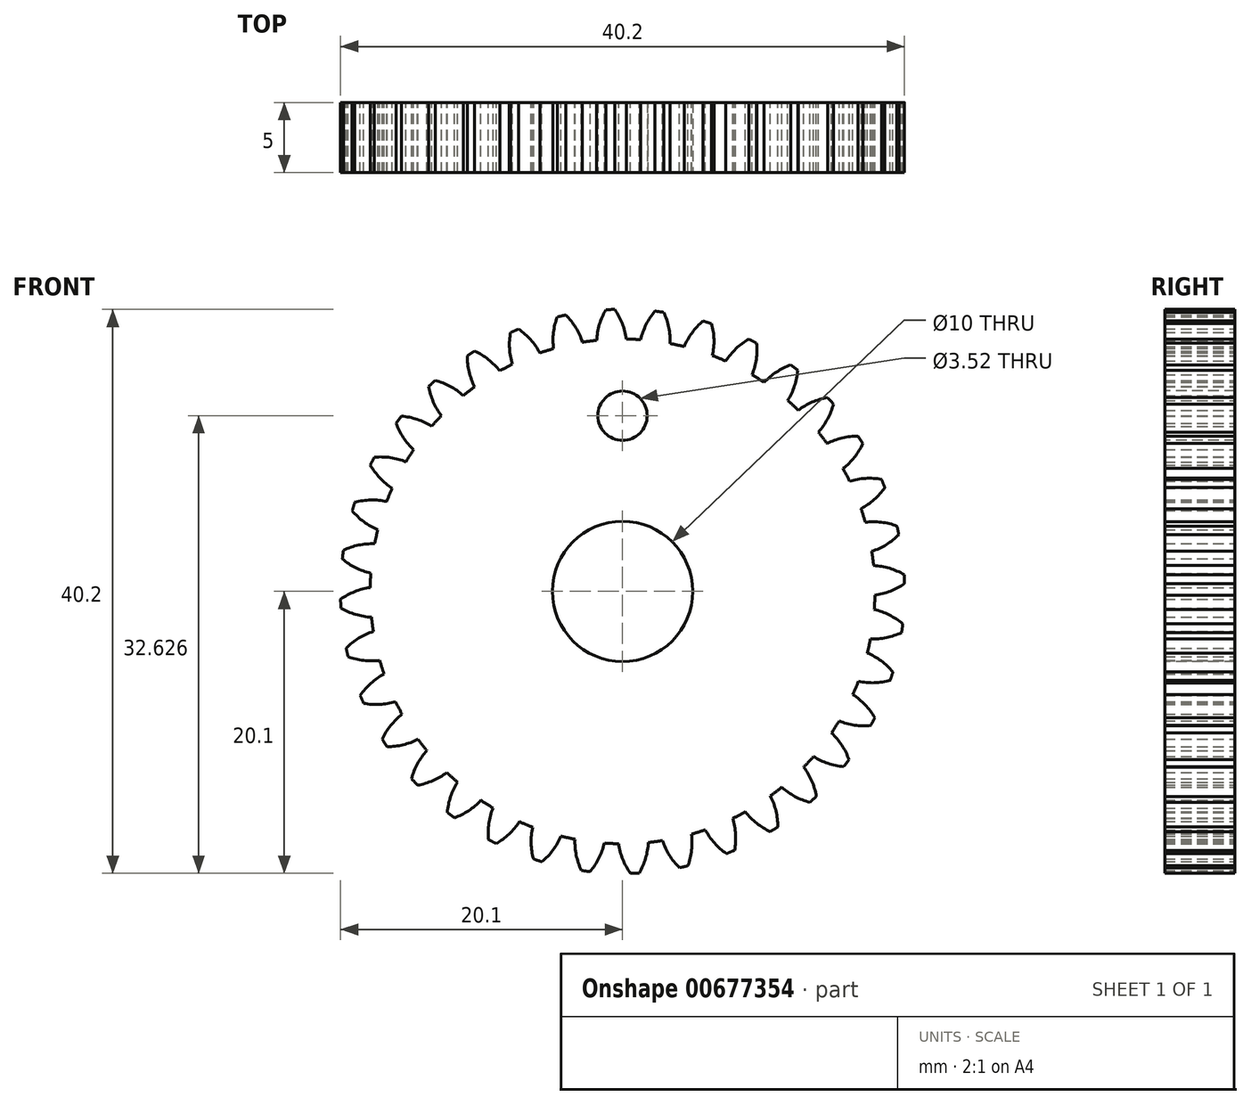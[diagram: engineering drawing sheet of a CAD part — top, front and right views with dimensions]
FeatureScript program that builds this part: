
annotation { "Feature Type Name" : "Feature", "Feature Type Description" : "" }
export const myFeature = defineFeature(function(context is Context, id is Id, definition is map)
    precondition{}
    {
        {
            var Q0;
            Q0=qCreatedBy(makeId("Front.planeOp"),FACE);
            var sketch = newSketch(context, id + "F0", { "sketchPlane" : qUnion([Q0])});
            skLineSegment(sketch, "E0", {"start": v(0, 0) * mm, "end": v(-1.18, 26.95) * mm, "construction": true});
            skArc(sketch, "E1.trimOffspring", {"start": v(0.27, 17.99) * mm, "mid": v(-0.02, 19.1) * mm, "end": v(-0.56, 20.1) * mm});
            skArc(sketch, "E2", {"start": v(-0.56, 20.1) * mm, "mid": v(-0.72, 20.1) * mm, "end": v(-0.88, 20.09) * mm});
            skArc(sketch, "E3.MirrorCS", {"start": v(-1.2, 20.07) * mm, "mid": v(-1.03, 20.08) * mm, "end": v(-0.88, 20.09) * mm});
            skArc(sketch, "E4.MirrorCS", {"start": v(-1.84, 17.9) * mm, "mid": v(-1.65, 19.02) * mm, "end": v(-1.2, 20.07) * mm});
            skArc(sketch, "E5.1.0", {"start": v(-2.85, 17.76) * mm, "mid": v(-3.33, 18.8) * mm, "end": v(-4.05, 19.7) * mm});
            skArc(sketch, "E5.1.1", {"start": v(-4.05, 19.7) * mm, "mid": v(-4.2, 19.66) * mm, "end": v(-4.35, 19.63) * mm});
            skArc(sketch, "E5.1.2", {"start": v(-4.92, 17.3) * mm, "mid": v(-4.93, 18.45) * mm, "end": v(-4.66, 19.56) * mm});
            skArc(sketch, "E5.1.3", {"start": v(-4.66, 19.56) * mm, "mid": v(-4.5, 19.6) * mm, "end": v(-4.35, 19.63) * mm});
            skArc(sketch, "E5.2.0", {"start": v(-5.9, 17) * mm, "mid": v(-6.55, 17.94) * mm, "end": v(-7.4, 18.7) * mm});
            skArc(sketch, "E5.2.1", {"start": v(-7.4, 18.7) * mm, "mid": v(-7.55, 18.64) * mm, "end": v(-7.7, 18.58) * mm});
            skArc(sketch, "E5.2.2", {"start": v(-7.85, 16.19) * mm, "mid": v(-8.05, 17.31) * mm, "end": v(-7.98, 18.46) * mm});
            skArc(sketch, "E5.2.3", {"start": v(-7.98, 18.46) * mm, "mid": v(-7.84, 18.52) * mm, "end": v(-7.7, 18.58) * mm});
            skArc(sketch, "E5.3.0", {"start": v(-8.76, 15.71) * mm, "mid": v(-9.56, 16.53) * mm, "end": v(-10.54, 17.13) * mm});
            skArc(sketch, "E5.3.1", {"start": v(-10.54, 17.13) * mm, "mid": v(-10.67, 17.04) * mm, "end": v(-10.8, 16.96) * mm});
            skArc(sketch, "E5.3.2", {"start": v(-10.54, 14.58) * mm, "mid": v(-10.94, 15.65) * mm, "end": v(-11.07, 16.79) * mm});
            skArc(sketch, "E5.3.3", {"start": v(-11.07, 16.79) * mm, "mid": v(-10.94, 16.87) * mm, "end": v(-10.8, 16.96) * mm});
            skArc(sketch, "E5.4.0", {"start": v(-11.35, 13.96) * mm, "mid": v(-12.29, 14.62) * mm, "end": v(-13.35, 15.04) * mm});
            skArc(sketch, "E5.4.1", {"start": v(-13.35, 15.04) * mm, "mid": v(-13.47, 14.93) * mm, "end": v(-13.58, 14.83) * mm});
            skArc(sketch, "E5.4.2", {"start": v(-12.91, 12.53) * mm, "mid": v(-13.49, 13.51) * mm, "end": v(-13.81, 14.61) * mm});
            skArc(sketch, "E5.4.3", {"start": v(-13.81, 14.61) * mm, "mid": v(-13.7, 14.72) * mm, "end": v(-13.58, 14.83) * mm});
            skArc(sketch, "E5.5.0", {"start": v(-13.6, 11.77) * mm, "mid": v(-14.64, 12.26) * mm, "end": v(-15.76, 12.49) * mm});
            skArc(sketch, "E5.5.1", {"start": v(-15.76, 12.49) * mm, "mid": v(-15.86, 12.37) * mm, "end": v(-15.95, 12.24) * mm});
            skArc(sketch, "E5.5.2", {"start": v(-14.9, 10.1) * mm, "mid": v(-15.63, 10.97) * mm, "end": v(-16.14, 12) * mm});
            skArc(sketch, "E5.5.3", {"start": v(-16.14, 12) * mm, "mid": v(-16.05, 12.12) * mm, "end": v(-15.95, 12.24) * mm});
            skArc(sketch, "E5.6.0", {"start": v(-15.44, 9.23) * mm, "mid": v(-16.55, 9.53) * mm, "end": v(-17.69, 9.56) * mm});
            skArc(sketch, "E5.6.1", {"start": v(-17.69, 9.56) * mm, "mid": v(-17.76, 9.42) * mm, "end": v(-17.84, 9.28) * mm});
            skArc(sketch, "E5.6.2", {"start": v(-16.42, 7.35) * mm, "mid": v(-17.3, 8.09) * mm, "end": v(-17.98, 9) * mm});
            skArc(sketch, "E5.6.3", {"start": v(-17.98, 9) * mm, "mid": v(-17.9, 9.15) * mm, "end": v(-17.84, 9.28) * mm});
            skArc(sketch, "E5.7.0", {"start": v(-16.8, 6.4) * mm, "mid": v(-17.95, 6.51) * mm, "end": v(-19.08, 6.34) * mm});
            skArc(sketch, "E5.7.1", {"start": v(-19.08, 6.34) * mm, "mid": v(-19.13, 6.2) * mm, "end": v(-19.18, 6.05) * mm});
            skArc(sketch, "E5.7.2", {"start": v(-17.45, 4.4) * mm, "mid": v(-18.44, 4.96) * mm, "end": v(-19.27, 5.75) * mm});
            skArc(sketch, "E5.7.3", {"start": v(-19.27, 5.75) * mm, "mid": v(-19.22, 5.9) * mm, "end": v(-19.18, 6.05) * mm});
            skArc(sketch, "E5.8.0", {"start": v(-17.67, 3.4) * mm, "mid": v(-18.8, 3.3) * mm, "end": v(-19.9, 2.94) * mm});
            skArc(sketch, "E5.8.1", {"start": v(-19.9, 2.94) * mm, "mid": v(-19.92, 2.78) * mm, "end": v(-19.94, 2.62) * mm});
            skArc(sketch, "E5.8.2", {"start": v(-17.94, 1.3) * mm, "mid": v(-19.02, 1.68) * mm, "end": v(-19.97, 2.31) * mm});
            skArc(sketch, "E5.8.3", {"start": v(-19.97, 2.31) * mm, "mid": v(-19.96, 2.47) * mm, "end": v(-19.94, 2.62) * mm});
            skArc(sketch, "E5.9.0", {"start": v(-17.99, 0.27) * mm, "mid": v(-19.1, -0.02) * mm, "end": v(-20.1, -0.56) * mm});
            skArc(sketch, "E5.9.1", {"start": v(-20.1, -0.56) * mm, "mid": v(-20.1, -0.72) * mm, "end": v(-20.09, -0.88) * mm});
            skArc(sketch, "E5.9.2", {"start": v(-17.9, -1.84) * mm, "mid": v(-19.02, -1.65) * mm, "end": v(-20.07, -1.2) * mm});
            skArc(sketch, "E5.9.3", {"start": v(-20.07, -1.2) * mm, "mid": v(-20.08, -1.03) * mm, "end": v(-20.09, -0.88) * mm});
            skArc(sketch, "E5.10.0", {"start": v(-17.76, -2.85) * mm, "mid": v(-18.8, -3.33) * mm, "end": v(-19.7, -4.05) * mm});
            skArc(sketch, "E5.10.1", {"start": v(-19.7, -4.05) * mm, "mid": v(-19.66, -4.2) * mm, "end": v(-19.63, -4.35) * mm});
            skArc(sketch, "E5.10.2", {"start": v(-17.3, -4.92) * mm, "mid": v(-18.45, -4.93) * mm, "end": v(-19.56, -4.66) * mm});
            skArc(sketch, "E5.10.3", {"start": v(-19.56, -4.66) * mm, "mid": v(-19.6, -4.5) * mm, "end": v(-19.63, -4.35) * mm});
            skArc(sketch, "E5.11.0", {"start": v(-17, -5.9) * mm, "mid": v(-17.94, -6.55) * mm, "end": v(-18.7, -7.4) * mm});
            skArc(sketch, "E5.11.1", {"start": v(-18.7, -7.4) * mm, "mid": v(-18.64, -7.55) * mm, "end": v(-18.58, -7.7) * mm});
            skArc(sketch, "E5.11.2", {"start": v(-16.19, -7.85) * mm, "mid": v(-17.31, -8.05) * mm, "end": v(-18.46, -7.98) * mm});
            skArc(sketch, "E5.11.3", {"start": v(-18.46, -7.98) * mm, "mid": v(-18.52, -7.84) * mm, "end": v(-18.58, -7.7) * mm});
            skArc(sketch, "E5.12.0", {"start": v(-15.71, -8.76) * mm, "mid": v(-16.53, -9.56) * mm, "end": v(-17.13, -10.54) * mm});
            skArc(sketch, "E5.12.1", {"start": v(-17.13, -10.54) * mm, "mid": v(-17.04, -10.67) * mm, "end": v(-16.96, -10.8) * mm});
            skArc(sketch, "E5.12.2", {"start": v(-14.58, -10.54) * mm, "mid": v(-15.65, -10.94) * mm, "end": v(-16.79, -11.07) * mm});
            skArc(sketch, "E5.12.3", {"start": v(-16.79, -11.07) * mm, "mid": v(-16.87, -10.94) * mm, "end": v(-16.96, -10.8) * mm});
            skArc(sketch, "E5.13.0", {"start": v(-13.96, -11.35) * mm, "mid": v(-14.62, -12.29) * mm, "end": v(-15.04, -13.35) * mm});
            skArc(sketch, "E5.13.1", {"start": v(-15.04, -13.35) * mm, "mid": v(-14.93, -13.47) * mm, "end": v(-14.83, -13.58) * mm});
            skArc(sketch, "E5.13.2", {"start": v(-12.53, -12.91) * mm, "mid": v(-13.51, -13.49) * mm, "end": v(-14.61, -13.81) * mm});
            skArc(sketch, "E5.13.3", {"start": v(-14.61, -13.81) * mm, "mid": v(-14.72, -13.7) * mm, "end": v(-14.83, -13.58) * mm});
            skArc(sketch, "E5.14.0", {"start": v(-11.77, -13.6) * mm, "mid": v(-12.26, -14.64) * mm, "end": v(-12.49, -15.76) * mm});
            skArc(sketch, "E5.14.1", {"start": v(-12.49, -15.76) * mm, "mid": v(-12.37, -15.86) * mm, "end": v(-12.24, -15.95) * mm});
            skArc(sketch, "E5.14.2", {"start": v(-10.1, -14.9) * mm, "mid": v(-10.97, -15.63) * mm, "end": v(-12, -16.14) * mm});
            skArc(sketch, "E5.14.3", {"start": v(-12, -16.14) * mm, "mid": v(-12.12, -16.05) * mm, "end": v(-12.24, -15.95) * mm});
            skArc(sketch, "E5.15.0", {"start": v(-9.23, -15.44) * mm, "mid": v(-9.53, -16.55) * mm, "end": v(-9.56, -17.69) * mm});
            skArc(sketch, "E5.15.1", {"start": v(-9.56, -17.69) * mm, "mid": v(-9.42, -17.76) * mm, "end": v(-9.28, -17.84) * mm});
            skArc(sketch, "E5.15.2", {"start": v(-7.35, -16.42) * mm, "mid": v(-8.09, -17.3) * mm, "end": v(-9, -17.98) * mm});
            skArc(sketch, "E5.15.3", {"start": v(-9, -17.98) * mm, "mid": v(-9.15, -17.9) * mm, "end": v(-9.28, -17.84) * mm});
            skArc(sketch, "E5.16.0", {"start": v(-6.4, -16.8) * mm, "mid": v(-6.51, -17.95) * mm, "end": v(-6.34, -19.08) * mm});
            skArc(sketch, "E5.16.1", {"start": v(-6.34, -19.08) * mm, "mid": v(-6.2, -19.13) * mm, "end": v(-6.05, -19.18) * mm});
            skArc(sketch, "E5.16.2", {"start": v(-4.4, -17.45) * mm, "mid": v(-4.96, -18.44) * mm, "end": v(-5.75, -19.27) * mm});
            skArc(sketch, "E5.16.3", {"start": v(-5.75, -19.27) * mm, "mid": v(-5.9, -19.22) * mm, "end": v(-6.05, -19.18) * mm});
            skArc(sketch, "E5.17.0", {"start": v(-3.4, -17.67) * mm, "mid": v(-3.3, -18.8) * mm, "end": v(-2.94, -19.9) * mm});
            skArc(sketch, "E5.17.1", {"start": v(-2.94, -19.9) * mm, "mid": v(-2.78, -19.92) * mm, "end": v(-2.62, -19.94) * mm});
            skArc(sketch, "E5.17.2", {"start": v(-1.3, -17.94) * mm, "mid": v(-1.68, -19.02) * mm, "end": v(-2.31, -19.97) * mm});
            skArc(sketch, "E5.17.3", {"start": v(-2.31, -19.97) * mm, "mid": v(-2.47, -19.96) * mm, "end": v(-2.62, -19.94) * mm});
            skArc(sketch, "E5.18.0", {"start": v(-0.27, -17.99) * mm, "mid": v(0.02, -19.1) * mm, "end": v(0.56, -20.1) * mm});
            skArc(sketch, "E5.18.1", {"start": v(0.56, -20.1) * mm, "mid": v(0.72, -20.1) * mm, "end": v(0.88, -20.09) * mm});
            skArc(sketch, "E5.18.2", {"start": v(1.84, -17.9) * mm, "mid": v(1.65, -19.02) * mm, "end": v(1.2, -20.07) * mm});
            skArc(sketch, "E5.18.3", {"start": v(1.2, -20.07) * mm, "mid": v(1.03, -20.08) * mm, "end": v(0.88, -20.09) * mm});
            skArc(sketch, "E5.19.0", {"start": v(2.85, -17.76) * mm, "mid": v(3.33, -18.8) * mm, "end": v(4.05, -19.7) * mm});
            skArc(sketch, "E5.19.1", {"start": v(4.05, -19.7) * mm, "mid": v(4.2, -19.66) * mm, "end": v(4.35, -19.63) * mm});
            skArc(sketch, "E5.19.2", {"start": v(4.92, -17.3) * mm, "mid": v(4.93, -18.45) * mm, "end": v(4.66, -19.56) * mm});
            skArc(sketch, "E5.19.3", {"start": v(4.66, -19.56) * mm, "mid": v(4.5, -19.6) * mm, "end": v(4.35, -19.63) * mm});
            skArc(sketch, "E5.20.0", {"start": v(5.9, -17) * mm, "mid": v(6.55, -17.94) * mm, "end": v(7.4, -18.7) * mm});
            skArc(sketch, "E5.20.1", {"start": v(7.4, -18.7) * mm, "mid": v(7.55, -18.64) * mm, "end": v(7.7, -18.58) * mm});
            skArc(sketch, "E5.20.2", {"start": v(7.85, -16.19) * mm, "mid": v(8.05, -17.31) * mm, "end": v(7.98, -18.46) * mm});
            skArc(sketch, "E5.20.3", {"start": v(7.98, -18.46) * mm, "mid": v(7.84, -18.52) * mm, "end": v(7.7, -18.58) * mm});
            skArc(sketch, "E5.21.0", {"start": v(8.76, -15.71) * mm, "mid": v(9.56, -16.53) * mm, "end": v(10.54, -17.13) * mm});
            skArc(sketch, "E5.21.1", {"start": v(10.54, -17.13) * mm, "mid": v(10.67, -17.04) * mm, "end": v(10.8, -16.96) * mm});
            skArc(sketch, "E5.21.2", {"start": v(10.54, -14.58) * mm, "mid": v(10.94, -15.65) * mm, "end": v(11.07, -16.79) * mm});
            skArc(sketch, "E5.21.3", {"start": v(11.07, -16.79) * mm, "mid": v(10.94, -16.87) * mm, "end": v(10.8, -16.96) * mm});
            skArc(sketch, "E5.22.0", {"start": v(11.35, -13.96) * mm, "mid": v(12.29, -14.62) * mm, "end": v(13.35, -15.04) * mm});
            skArc(sketch, "E5.22.1", {"start": v(13.35, -15.04) * mm, "mid": v(13.47, -14.93) * mm, "end": v(13.58, -14.83) * mm});
            skArc(sketch, "E5.22.2", {"start": v(12.91, -12.53) * mm, "mid": v(13.49, -13.51) * mm, "end": v(13.81, -14.61) * mm});
            skArc(sketch, "E5.22.3", {"start": v(13.81, -14.61) * mm, "mid": v(13.7, -14.72) * mm, "end": v(13.58, -14.83) * mm});
            skArc(sketch, "E5.23.0", {"start": v(13.6, -11.77) * mm, "mid": v(14.64, -12.26) * mm, "end": v(15.76, -12.49) * mm});
            skArc(sketch, "E5.23.1", {"start": v(15.76, -12.49) * mm, "mid": v(15.86, -12.37) * mm, "end": v(15.95, -12.24) * mm});
            skArc(sketch, "E5.23.2", {"start": v(14.9, -10.1) * mm, "mid": v(15.63, -10.97) * mm, "end": v(16.14, -12) * mm});
            skArc(sketch, "E5.23.3", {"start": v(16.14, -12) * mm, "mid": v(16.05, -12.12) * mm, "end": v(15.95, -12.24) * mm});
            skArc(sketch, "E5.24.0", {"start": v(15.44, -9.23) * mm, "mid": v(16.55, -9.53) * mm, "end": v(17.69, -9.56) * mm});
            skArc(sketch, "E5.24.1", {"start": v(17.69, -9.56) * mm, "mid": v(17.76, -9.42) * mm, "end": v(17.84, -9.28) * mm});
            skArc(sketch, "E5.24.2", {"start": v(16.42, -7.35) * mm, "mid": v(17.3, -8.09) * mm, "end": v(17.98, -9) * mm});
            skArc(sketch, "E5.24.3", {"start": v(17.98, -9) * mm, "mid": v(17.9, -9.15) * mm, "end": v(17.84, -9.28) * mm});
            skArc(sketch, "E5.25.0", {"start": v(16.8, -6.4) * mm, "mid": v(17.95, -6.51) * mm, "end": v(19.08, -6.34) * mm});
            skArc(sketch, "E5.25.1", {"start": v(19.08, -6.34) * mm, "mid": v(19.13, -6.2) * mm, "end": v(19.18, -6.05) * mm});
            skArc(sketch, "E5.25.2", {"start": v(17.45, -4.4) * mm, "mid": v(18.44, -4.96) * mm, "end": v(19.27, -5.75) * mm});
            skArc(sketch, "E5.25.3", {"start": v(19.27, -5.75) * mm, "mid": v(19.22, -5.9) * mm, "end": v(19.18, -6.05) * mm});
            skArc(sketch, "E5.26.0", {"start": v(17.67, -3.4) * mm, "mid": v(18.8, -3.3) * mm, "end": v(19.9, -2.94) * mm});
            skArc(sketch, "E5.26.1", {"start": v(19.9, -2.94) * mm, "mid": v(19.92, -2.78) * mm, "end": v(19.94, -2.62) * mm});
            skArc(sketch, "E5.26.2", {"start": v(17.94, -1.3) * mm, "mid": v(19.02, -1.68) * mm, "end": v(19.97, -2.31) * mm});
            skArc(sketch, "E5.26.3", {"start": v(19.97, -2.31) * mm, "mid": v(19.96, -2.47) * mm, "end": v(19.94, -2.62) * mm});
            skArc(sketch, "E5.27.0", {"start": v(17.99, -0.27) * mm, "mid": v(19.1, 0.02) * mm, "end": v(20.1, 0.56) * mm});
            skArc(sketch, "E5.27.1", {"start": v(20.1, 0.56) * mm, "mid": v(20.1, 0.72) * mm, "end": v(20.09, 0.88) * mm});
            skArc(sketch, "E5.27.2", {"start": v(17.9, 1.84) * mm, "mid": v(19.02, 1.65) * mm, "end": v(20.07, 1.2) * mm});
            skArc(sketch, "E5.27.3", {"start": v(20.07, 1.2) * mm, "mid": v(20.08, 1.03) * mm, "end": v(20.09, 0.88) * mm});
            skArc(sketch, "E5.28.0", {"start": v(17.76, 2.85) * mm, "mid": v(18.8, 3.33) * mm, "end": v(19.7, 4.05) * mm});
            skArc(sketch, "E5.28.1", {"start": v(19.7, 4.05) * mm, "mid": v(19.66, 4.2) * mm, "end": v(19.63, 4.35) * mm});
            skArc(sketch, "E5.28.2", {"start": v(17.3, 4.92) * mm, "mid": v(18.45, 4.93) * mm, "end": v(19.56, 4.66) * mm});
            skArc(sketch, "E5.28.3", {"start": v(19.56, 4.66) * mm, "mid": v(19.6, 4.5) * mm, "end": v(19.63, 4.35) * mm});
            skArc(sketch, "E5.29.0", {"start": v(17, 5.9) * mm, "mid": v(17.94, 6.55) * mm, "end": v(18.7, 7.4) * mm});
            skArc(sketch, "E5.29.1", {"start": v(18.7, 7.4) * mm, "mid": v(18.64, 7.55) * mm, "end": v(18.58, 7.7) * mm});
            skArc(sketch, "E5.29.2", {"start": v(16.19, 7.85) * mm, "mid": v(17.31, 8.05) * mm, "end": v(18.46, 7.98) * mm});
            skArc(sketch, "E5.29.3", {"start": v(18.46, 7.98) * mm, "mid": v(18.52, 7.84) * mm, "end": v(18.58, 7.7) * mm});
            skArc(sketch, "E5.30.0", {"start": v(15.71, 8.76) * mm, "mid": v(16.53, 9.56) * mm, "end": v(17.13, 10.54) * mm});
            skArc(sketch, "E5.30.1", {"start": v(17.13, 10.54) * mm, "mid": v(17.04, 10.67) * mm, "end": v(16.96, 10.8) * mm});
            skArc(sketch, "E5.30.2", {"start": v(14.58, 10.54) * mm, "mid": v(15.65, 10.94) * mm, "end": v(16.79, 11.07) * mm});
            skArc(sketch, "E5.30.3", {"start": v(16.79, 11.07) * mm, "mid": v(16.87, 10.94) * mm, "end": v(16.96, 10.8) * mm});
            skArc(sketch, "E5.31.0", {"start": v(13.96, 11.35) * mm, "mid": v(14.62, 12.29) * mm, "end": v(15.04, 13.35) * mm});
            skArc(sketch, "E5.31.1", {"start": v(15.04, 13.35) * mm, "mid": v(14.93, 13.47) * mm, "end": v(14.83, 13.58) * mm});
            skArc(sketch, "E5.31.2", {"start": v(12.53, 12.91) * mm, "mid": v(13.51, 13.49) * mm, "end": v(14.61, 13.81) * mm});
            skArc(sketch, "E5.31.3", {"start": v(14.61, 13.81) * mm, "mid": v(14.72, 13.7) * mm, "end": v(14.83, 13.58) * mm});
            skArc(sketch, "E5.32.0", {"start": v(11.77, 13.6) * mm, "mid": v(12.26, 14.64) * mm, "end": v(12.49, 15.76) * mm});
            skArc(sketch, "E5.32.1", {"start": v(12.49, 15.76) * mm, "mid": v(12.37, 15.86) * mm, "end": v(12.24, 15.95) * mm});
            skArc(sketch, "E5.32.2", {"start": v(10.1, 14.9) * mm, "mid": v(10.97, 15.63) * mm, "end": v(12, 16.14) * mm});
            skArc(sketch, "E5.32.3", {"start": v(12, 16.14) * mm, "mid": v(12.12, 16.05) * mm, "end": v(12.24, 15.95) * mm});
            skArc(sketch, "E5.33.0", {"start": v(9.23, 15.44) * mm, "mid": v(9.53, 16.55) * mm, "end": v(9.56, 17.69) * mm});
            skArc(sketch, "E5.33.1", {"start": v(9.56, 17.69) * mm, "mid": v(9.42, 17.76) * mm, "end": v(9.28, 17.84) * mm});
            skArc(sketch, "E5.33.2", {"start": v(7.35, 16.42) * mm, "mid": v(8.09, 17.3) * mm, "end": v(9, 17.98) * mm});
            skArc(sketch, "E5.33.3", {"start": v(9, 17.98) * mm, "mid": v(9.15, 17.9) * mm, "end": v(9.28, 17.84) * mm});
            skArc(sketch, "E5.34.0", {"start": v(6.4, 16.8) * mm, "mid": v(6.51, 17.95) * mm, "end": v(6.34, 19.08) * mm});
            skArc(sketch, "E5.34.1", {"start": v(6.34, 19.08) * mm, "mid": v(6.2, 19.13) * mm, "end": v(6.05, 19.18) * mm});
            skArc(sketch, "E5.34.2", {"start": v(4.4, 17.45) * mm, "mid": v(4.96, 18.44) * mm, "end": v(5.75, 19.27) * mm});
            skArc(sketch, "E5.34.3", {"start": v(5.75, 19.27) * mm, "mid": v(5.9, 19.22) * mm, "end": v(6.05, 19.18) * mm});
            skArc(sketch, "E5.35.0", {"start": v(3.4, 17.67) * mm, "mid": v(3.3, 18.8) * mm, "end": v(2.94, 19.9) * mm});
            skArc(sketch, "E5.35.1", {"start": v(2.94, 19.9) * mm, "mid": v(2.78, 19.92) * mm, "end": v(2.62, 19.94) * mm});
            skArc(sketch, "E5.35.2", {"start": v(1.3, 17.94) * mm, "mid": v(1.68, 19.02) * mm, "end": v(2.31, 19.97) * mm});
            skArc(sketch, "E5.35.3", {"start": v(2.31, 19.97) * mm, "mid": v(2.47, 19.96) * mm, "end": v(2.62, 19.94) * mm});
            skArc(sketch, "E6", {"start": v(-4.92, 17.3) * mm, "mid": v(-5.4, 17.16) * mm, "end": v(-5.9, 17) * mm});
            skArc(sketch, "E7.trimOffspring", {"start": v(-1.84, 17.9) * mm, "mid": v(-2.35, 17.84) * mm, "end": v(-2.85, 17.76) * mm});
            skArc(sketch, "E8.trimOffspring", {"start": v(1.3, 17.94) * mm, "mid": v(0.78, 17.97) * mm, "end": v(0.27, 17.99) * mm});
            skArc(sketch, "E9.trimOffspring", {"start": v(4.4, 17.45) * mm, "mid": v(3.9, 17.56) * mm, "end": v(3.4, 17.67) * mm});
            skArc(sketch, "E10.trimOffspring", {"start": v(7.35, 16.42) * mm, "mid": v(6.88, 16.62) * mm, "end": v(6.4, 16.8) * mm});
            skArc(sketch, "E11.trimOffspring", {"start": v(10.1, 14.9) * mm, "mid": v(9.67, 15.17) * mm, "end": v(9.23, 15.44) * mm});
            skArc(sketch, "E12.trimOffspring", {"start": v(12.53, 12.91) * mm, "mid": v(12.15, 13.26) * mm, "end": v(11.77, 13.6) * mm});
            skArc(sketch, "E13.trimOffspring", {"start": v(16.19, 7.85) * mm, "mid": v(15.96, 8.3) * mm, "end": v(15.71, 8.76) * mm});
            skArc(sketch, "E14.trimOffspring", {"start": v(17.3, 4.92) * mm, "mid": v(17.16, 5.4) * mm, "end": v(17, 5.9) * mm});
            skArc(sketch, "E15.trimOffspring", {"start": v(14.58, 10.54) * mm, "mid": v(14.27, 10.95) * mm, "end": v(13.96, 11.35) * mm});
            skArc(sketch, "E16.trimOffspring", {"start": v(17.9, 1.84) * mm, "mid": v(17.84, 2.35) * mm, "end": v(17.76, 2.85) * mm});
            skArc(sketch, "E17.trimOffspring", {"start": v(17.94, -1.3) * mm, "mid": v(17.97, -0.78) * mm, "end": v(17.99, -0.27) * mm});
            skArc(sketch, "E18.trimOffspring", {"start": v(17.45, -4.4) * mm, "mid": v(17.56, -3.9) * mm, "end": v(17.67, -3.4) * mm});
            skArc(sketch, "E19.trimOffspring", {"start": v(16.42, -7.35) * mm, "mid": v(16.62, -6.88) * mm, "end": v(16.8, -6.4) * mm});
            skArc(sketch, "E20.trimOffspring", {"start": v(14.9, -10.1) * mm, "mid": v(15.17, -9.67) * mm, "end": v(15.44, -9.23) * mm});
            skArc(sketch, "E21.trimOffspring", {"start": v(12.91, -12.53) * mm, "mid": v(13.26, -12.15) * mm, "end": v(13.6, -11.77) * mm});
            skArc(sketch, "E22.trimOffspring", {"start": v(10.54, -14.58) * mm, "mid": v(10.95, -14.27) * mm, "end": v(11.35, -13.96) * mm});
            skArc(sketch, "E23.trimOffspring", {"start": v(7.85, -16.19) * mm, "mid": v(8.3, -15.96) * mm, "end": v(8.76, -15.71) * mm});
            skArc(sketch, "E24.trimOffspring", {"start": v(4.92, -17.3) * mm, "mid": v(5.4, -17.16) * mm, "end": v(5.9, -17) * mm});
            skArc(sketch, "E25.trimOffspring", {"start": v(1.84, -17.9) * mm, "mid": v(2.35, -17.84) * mm, "end": v(2.85, -17.76) * mm});
            skArc(sketch, "E26.trimOffspring", {"start": v(-1.3, -17.94) * mm, "mid": v(-0.78, -17.97) * mm, "end": v(-0.27, -17.99) * mm});
            skArc(sketch, "E27.trimOffspring", {"start": v(-4.4, -17.45) * mm, "mid": v(-3.9, -17.56) * mm, "end": v(-3.4, -17.67) * mm});
            skArc(sketch, "E28.trimOffspring", {"start": v(-7.35, -16.42) * mm, "mid": v(-6.88, -16.62) * mm, "end": v(-6.4, -16.8) * mm});
            skArc(sketch, "E29.trimOffspring", {"start": v(-10.1, -14.9) * mm, "mid": v(-9.67, -15.17) * mm, "end": v(-9.23, -15.44) * mm});
            skArc(sketch, "E30.trimOffspring", {"start": v(-12.53, -12.91) * mm, "mid": v(-12.15, -13.26) * mm, "end": v(-11.77, -13.6) * mm});
            skArc(sketch, "E31.trimOffspring", {"start": v(-14.58, -10.54) * mm, "mid": v(-14.27, -10.95) * mm, "end": v(-13.96, -11.35) * mm});
            skArc(sketch, "E32.trimOffspring", {"start": v(-16.19, -7.85) * mm, "mid": v(-15.96, -8.3) * mm, "end": v(-15.71, -8.76) * mm});
            skArc(sketch, "E33.trimOffspring", {"start": v(-17.3, -4.92) * mm, "mid": v(-17.16, -5.4) * mm, "end": v(-17, -5.9) * mm});
            skArc(sketch, "E34.trimOffspring", {"start": v(-17.9, -1.84) * mm, "mid": v(-17.84, -2.35) * mm, "end": v(-17.76, -2.85) * mm});
            skArc(sketch, "E35.trimOffspring", {"start": v(-17.94, 1.3) * mm, "mid": v(-17.97, 0.78) * mm, "end": v(-17.99, 0.27) * mm});
            skArc(sketch, "E36.trimOffspring", {"start": v(-17.45, 4.4) * mm, "mid": v(-17.56, 3.9) * mm, "end": v(-17.67, 3.4) * mm});
            skArc(sketch, "E37.trimOffspring", {"start": v(-16.42, 7.35) * mm, "mid": v(-16.62, 6.88) * mm, "end": v(-16.8, 6.4) * mm});
            skArc(sketch, "E38.trimOffspring", {"start": v(-14.9, 10.1) * mm, "mid": v(-15.17, 9.67) * mm, "end": v(-15.44, 9.23) * mm});
            skArc(sketch, "E39.trimOffspring", {"start": v(-12.91, 12.53) * mm, "mid": v(-13.26, 12.15) * mm, "end": v(-13.6, 11.77) * mm});
            skArc(sketch, "E40.trimOffspring", {"start": v(-10.54, 14.58) * mm, "mid": v(-10.95, 14.27) * mm, "end": v(-11.35, 13.96) * mm});
            skArc(sketch, "E41.trimOffspring", {"start": v(-7.85, 16.19) * mm, "mid": v(-8.3, 15.96) * mm, "end": v(-8.76, 15.71) * mm});
            skSolve(sketch);
        }
        {
            var Q0;
            Q0=makeQuery(id+"F0.imprint","IMPRINT",FACE,{"disambiguationData":[TD([[makeQuery(id+"F0.imprint","IMPRINT",EDGE,{"derivedFrom":sQuery(id+"F0.wireOp",EDGE,"E1.trimOffspring")}),1.0]])]});
            extrude(context, id + "F1", {"entities" : qUnion([Q0]), "depth" : 5 * mm, "offsetDistance" : 25 * mm});
        }
        {
            var Q0;
            Q0=makeQuery(id+"F1.opExtrude","CAP_FACE",FACE,{"disambiguationData":[OSD([sQuery(id+"F0.wireOp",EDGE,"E1.trimOffspring"),sQuery(id+"F0.wireOp",EDGE,"E2"),sQuery(id+"F0.wireOp",EDGE,"E3.MirrorCS"),sQuery(id+"F0.wireOp",EDGE,"E4.MirrorCS"),sQuery(id+"F0.wireOp",EDGE,"E5.1.0"),sQuery(id+"F0.wireOp",EDGE,"E5.1.1"),sQuery(id+"F0.wireOp",EDGE,"E5.1.2"),sQuery(id+"F0.wireOp",EDGE,"E5.1.3"),sQuery(id+"F0.wireOp",EDGE,"E5.2.0"),sQuery(id+"F0.wireOp",EDGE,"E5.2.1"),sQuery(id+"F0.wireOp",EDGE,"E5.2.2"),sQuery(id+"F0.wireOp",EDGE,"E5.2.3"),sQuery(id+"F0.wireOp",EDGE,"E5.3.0"),sQuery(id+"F0.wireOp",EDGE,"E5.3.1"),sQuery(id+"F0.wireOp",EDGE,"E5.3.2"),sQuery(id+"F0.wireOp",EDGE,"E5.3.3"),sQuery(id+"F0.wireOp",EDGE,"E5.4.0"),sQuery(id+"F0.wireOp",EDGE,"E5.4.1"),sQuery(id+"F0.wireOp",EDGE,"E5.4.2"),sQuery(id+"F0.wireOp",EDGE,"E5.4.3"),sQuery(id+"F0.wireOp",EDGE,"E5.5.0"),sQuery(id+"F0.wireOp",EDGE,"E5.5.1"),sQuery(id+"F0.wireOp",EDGE,"E5.5.2"),sQuery(id+"F0.wireOp",EDGE,"E5.5.3"),sQuery(id+"F0.wireOp",EDGE,"E5.6.0"),sQuery(id+"F0.wireOp",EDGE,"E5.6.1"),sQuery(id+"F0.wireOp",EDGE,"E5.6.2"),sQuery(id+"F0.wireOp",EDGE,"E5.6.3"),sQuery(id+"F0.wireOp",EDGE,"E5.7.0"),sQuery(id+"F0.wireOp",EDGE,"E5.7.1"),sQuery(id+"F0.wireOp",EDGE,"E5.7.2"),sQuery(id+"F0.wireOp",EDGE,"E5.7.3"),sQuery(id+"F0.wireOp",EDGE,"E5.8.0"),sQuery(id+"F0.wireOp",EDGE,"E5.8.1"),sQuery(id+"F0.wireOp",EDGE,"E5.8.2"),sQuery(id+"F0.wireOp",EDGE,"E5.8.3"),sQuery(id+"F0.wireOp",EDGE,"E5.9.0"),sQuery(id+"F0.wireOp",EDGE,"E5.9.1"),sQuery(id+"F0.wireOp",EDGE,"E5.9.2"),sQuery(id+"F0.wireOp",EDGE,"E5.9.3"),sQuery(id+"F0.wireOp",EDGE,"E5.10.0"),sQuery(id+"F0.wireOp",EDGE,"E5.10.1"),sQuery(id+"F0.wireOp",EDGE,"E5.10.2"),sQuery(id+"F0.wireOp",EDGE,"E5.10.3"),sQuery(id+"F0.wireOp",EDGE,"E5.11.0"),sQuery(id+"F0.wireOp",EDGE,"E5.11.1"),sQuery(id+"F0.wireOp",EDGE,"E5.11.2"),sQuery(id+"F0.wireOp",EDGE,"E5.11.3"),sQuery(id+"F0.wireOp",EDGE,"E5.12.0"),sQuery(id+"F0.wireOp",EDGE,"E5.12.1"),sQuery(id+"F0.wireOp",EDGE,"E5.12.2"),sQuery(id+"F0.wireOp",EDGE,"E5.12.3"),sQuery(id+"F0.wireOp",EDGE,"E5.13.0"),sQuery(id+"F0.wireOp",EDGE,"E5.13.1"),sQuery(id+"F0.wireOp",EDGE,"E5.13.2"),sQuery(id+"F0.wireOp",EDGE,"E5.13.3"),sQuery(id+"F0.wireOp",EDGE,"E5.14.0"),sQuery(id+"F0.wireOp",EDGE,"E5.14.1"),sQuery(id+"F0.wireOp",EDGE,"E5.14.2"),sQuery(id+"F0.wireOp",EDGE,"E5.14.3"),sQuery(id+"F0.wireOp",EDGE,"E5.15.0"),sQuery(id+"F0.wireOp",EDGE,"E5.15.1"),sQuery(id+"F0.wireOp",EDGE,"E5.15.2"),sQuery(id+"F0.wireOp",EDGE,"E5.15.3"),sQuery(id+"F0.wireOp",EDGE,"E5.16.0"),sQuery(id+"F0.wireOp",EDGE,"E5.16.1"),sQuery(id+"F0.wireOp",EDGE,"E5.16.2"),sQuery(id+"F0.wireOp",EDGE,"E5.16.3"),sQuery(id+"F0.wireOp",EDGE,"E5.17.0"),sQuery(id+"F0.wireOp",EDGE,"E5.17.1"),sQuery(id+"F0.wireOp",EDGE,"E5.17.2"),sQuery(id+"F0.wireOp",EDGE,"E5.17.3"),sQuery(id+"F0.wireOp",EDGE,"E5.18.0"),sQuery(id+"F0.wireOp",EDGE,"E5.18.1"),sQuery(id+"F0.wireOp",EDGE,"E5.18.2"),sQuery(id+"F0.wireOp",EDGE,"E5.18.3"),sQuery(id+"F0.wireOp",EDGE,"E5.19.0"),sQuery(id+"F0.wireOp",EDGE,"E5.19.1"),sQuery(id+"F0.wireOp",EDGE,"E5.19.2"),sQuery(id+"F0.wireOp",EDGE,"E5.19.3"),sQuery(id+"F0.wireOp",EDGE,"E5.20.0"),sQuery(id+"F0.wireOp",EDGE,"E5.20.1"),sQuery(id+"F0.wireOp",EDGE,"E5.20.2"),sQuery(id+"F0.wireOp",EDGE,"E5.20.3"),sQuery(id+"F0.wireOp",EDGE,"E5.21.0"),sQuery(id+"F0.wireOp",EDGE,"E5.21.1"),sQuery(id+"F0.wireOp",EDGE,"E5.21.2"),sQuery(id+"F0.wireOp",EDGE,"E5.21.3"),sQuery(id+"F0.wireOp",EDGE,"E5.22.0"),sQuery(id+"F0.wireOp",EDGE,"E5.22.1"),sQuery(id+"F0.wireOp",EDGE,"E5.22.2"),sQuery(id+"F0.wireOp",EDGE,"E5.22.3"),sQuery(id+"F0.wireOp",EDGE,"E5.23.0"),sQuery(id+"F0.wireOp",EDGE,"E5.23.1"),sQuery(id+"F0.wireOp",EDGE,"E5.23.2"),sQuery(id+"F0.wireOp",EDGE,"E5.23.3"),sQuery(id+"F0.wireOp",EDGE,"E5.24.0"),sQuery(id+"F0.wireOp",EDGE,"E5.24.1"),sQuery(id+"F0.wireOp",EDGE,"E5.24.2"),sQuery(id+"F0.wireOp",EDGE,"E5.24.3"),sQuery(id+"F0.wireOp",EDGE,"E5.25.0"),sQuery(id+"F0.wireOp",EDGE,"E5.25.1"),sQuery(id+"F0.wireOp",EDGE,"E5.25.2"),sQuery(id+"F0.wireOp",EDGE,"E5.25.3"),sQuery(id+"F0.wireOp",EDGE,"E5.26.0"),sQuery(id+"F0.wireOp",EDGE,"E5.26.1"),sQuery(id+"F0.wireOp",EDGE,"E5.26.2"),sQuery(id+"F0.wireOp",EDGE,"E5.26.3"),sQuery(id+"F0.wireOp",EDGE,"E5.27.0"),sQuery(id+"F0.wireOp",EDGE,"E5.27.1"),sQuery(id+"F0.wireOp",EDGE,"E5.27.2"),sQuery(id+"F0.wireOp",EDGE,"E5.27.3"),sQuery(id+"F0.wireOp",EDGE,"E5.28.0"),sQuery(id+"F0.wireOp",EDGE,"E5.28.1"),sQuery(id+"F0.wireOp",EDGE,"E5.28.2"),sQuery(id+"F0.wireOp",EDGE,"E5.28.3"),sQuery(id+"F0.wireOp",EDGE,"E5.29.0"),sQuery(id+"F0.wireOp",EDGE,"E5.29.1"),sQuery(id+"F0.wireOp",EDGE,"E5.29.2"),sQuery(id+"F0.wireOp",EDGE,"E5.29.3"),sQuery(id+"F0.wireOp",EDGE,"E5.30.0"),sQuery(id+"F0.wireOp",EDGE,"E5.30.1"),sQuery(id+"F0.wireOp",EDGE,"E5.30.2"),sQuery(id+"F0.wireOp",EDGE,"E5.30.3"),sQuery(id+"F0.wireOp",EDGE,"E5.31.0"),sQuery(id+"F0.wireOp",EDGE,"E5.31.1"),sQuery(id+"F0.wireOp",EDGE,"E5.31.2"),sQuery(id+"F0.wireOp",EDGE,"E5.31.3"),sQuery(id+"F0.wireOp",EDGE,"E5.32.0"),sQuery(id+"F0.wireOp",EDGE,"E5.32.1"),sQuery(id+"F0.wireOp",EDGE,"E5.32.2"),sQuery(id+"F0.wireOp",EDGE,"E5.32.3"),sQuery(id+"F0.wireOp",EDGE,"E5.33.0"),sQuery(id+"F0.wireOp",EDGE,"E5.33.1"),sQuery(id+"F0.wireOp",EDGE,"E5.33.2"),sQuery(id+"F0.wireOp",EDGE,"E5.33.3"),sQuery(id+"F0.wireOp",EDGE,"E5.34.0"),sQuery(id+"F0.wireOp",EDGE,"E5.34.1"),sQuery(id+"F0.wireOp",EDGE,"E5.34.2"),sQuery(id+"F0.wireOp",EDGE,"E5.34.3"),sQuery(id+"F0.wireOp",EDGE,"E5.35.0"),sQuery(id+"F0.wireOp",EDGE,"E5.35.1"),sQuery(id+"F0.wireOp",EDGE,"E5.35.2"),sQuery(id+"F0.wireOp",EDGE,"E5.35.3"),sQuery(id+"F0.wireOp",EDGE,"E6"),sQuery(id+"F0.wireOp",EDGE,"E7.trimOffspring"),sQuery(id+"F0.wireOp",EDGE,"E8.trimOffspring"),sQuery(id+"F0.wireOp",EDGE,"E9.trimOffspring"),sQuery(id+"F0.wireOp",EDGE,"E10.trimOffspring"),sQuery(id+"F0.wireOp",EDGE,"E11.trimOffspring"),sQuery(id+"F0.wireOp",EDGE,"E12.trimOffspring"),sQuery(id+"F0.wireOp",EDGE,"E13.trimOffspring"),sQuery(id+"F0.wireOp",EDGE,"E14.trimOffspring"),sQuery(id+"F0.wireOp",EDGE,"E15.trimOffspring"),sQuery(id+"F0.wireOp",EDGE,"E16.trimOffspring"),sQuery(id+"F0.wireOp",EDGE,"E17.trimOffspring"),sQuery(id+"F0.wireOp",EDGE,"E18.trimOffspring"),sQuery(id+"F0.wireOp",EDGE,"E19.trimOffspring"),sQuery(id+"F0.wireOp",EDGE,"E20.trimOffspring"),sQuery(id+"F0.wireOp",EDGE,"E21.trimOffspring"),sQuery(id+"F0.wireOp",EDGE,"E22.trimOffspring"),sQuery(id+"F0.wireOp",EDGE,"E23.trimOffspring"),sQuery(id+"F0.wireOp",EDGE,"E24.trimOffspring"),sQuery(id+"F0.wireOp",EDGE,"E25.trimOffspring"),sQuery(id+"F0.wireOp",EDGE,"E26.trimOffspring"),sQuery(id+"F0.wireOp",EDGE,"E27.trimOffspring"),sQuery(id+"F0.wireOp",EDGE,"E28.trimOffspring"),sQuery(id+"F0.wireOp",EDGE,"E29.trimOffspring"),sQuery(id+"F0.wireOp",EDGE,"E30.trimOffspring"),sQuery(id+"F0.wireOp",EDGE,"E31.trimOffspring"),sQuery(id+"F0.wireOp",EDGE,"E32.trimOffspring"),sQuery(id+"F0.wireOp",EDGE,"E33.trimOffspring"),sQuery(id+"F0.wireOp",EDGE,"E34.trimOffspring"),sQuery(id+"F0.wireOp",EDGE,"E35.trimOffspring"),sQuery(id+"F0.wireOp",EDGE,"E36.trimOffspring"),sQuery(id+"F0.wireOp",EDGE,"E37.trimOffspring"),sQuery(id+"F0.wireOp",EDGE,"E38.trimOffspring"),sQuery(id+"F0.wireOp",EDGE,"E39.trimOffspring"),sQuery(id+"F0.wireOp",EDGE,"E40.trimOffspring"),sQuery(id+"F0.wireOp",EDGE,"E41.trimOffspring")])],"isStart":false});
            var sketch = newSketch(context, id + "F2", { "sketchPlane" : qUnion([Q0])});
            skCircle(sketch, "E42", {"center": v(0, 0) * mm, "radius": 5 * mm});
            skSolve(sketch);
        }
        {
            var Q0;
            Q0 = qSketchRegion(id + "F2", true);
            extrude(context, id + "F3", {"entities" : qUnion([Q0]), "operationType" : NewBodyOperationType.REMOVE, "endBound" : BoundingType.THROUGH_ALL, "oppositeDirection" : true, "depth" : 25 * mm, "offsetDistance" : 25 * mm});
        }
        {
            var Q0;
            Q0=makeQuery(id+"F1.opExtrude","CAP_FACE",FACE,{"disambiguationData":[OSD([sQuery(id+"F0.wireOp",EDGE,"E1.trimOffspring"),sQuery(id+"F0.wireOp",EDGE,"E2"),sQuery(id+"F0.wireOp",EDGE,"E3.MirrorCS"),sQuery(id+"F0.wireOp",EDGE,"E4.MirrorCS"),sQuery(id+"F0.wireOp",EDGE,"E5.1.0"),sQuery(id+"F0.wireOp",EDGE,"E5.1.1"),sQuery(id+"F0.wireOp",EDGE,"E5.1.2"),sQuery(id+"F0.wireOp",EDGE,"E5.1.3"),sQuery(id+"F0.wireOp",EDGE,"E5.2.0"),sQuery(id+"F0.wireOp",EDGE,"E5.2.1"),sQuery(id+"F0.wireOp",EDGE,"E5.2.2"),sQuery(id+"F0.wireOp",EDGE,"E5.2.3"),sQuery(id+"F0.wireOp",EDGE,"E5.3.0"),sQuery(id+"F0.wireOp",EDGE,"E5.3.1"),sQuery(id+"F0.wireOp",EDGE,"E5.3.2"),sQuery(id+"F0.wireOp",EDGE,"E5.3.3"),sQuery(id+"F0.wireOp",EDGE,"E5.4.0"),sQuery(id+"F0.wireOp",EDGE,"E5.4.1"),sQuery(id+"F0.wireOp",EDGE,"E5.4.2"),sQuery(id+"F0.wireOp",EDGE,"E5.4.3"),sQuery(id+"F0.wireOp",EDGE,"E5.5.0"),sQuery(id+"F0.wireOp",EDGE,"E5.5.1"),sQuery(id+"F0.wireOp",EDGE,"E5.5.2"),sQuery(id+"F0.wireOp",EDGE,"E5.5.3"),sQuery(id+"F0.wireOp",EDGE,"E5.6.0"),sQuery(id+"F0.wireOp",EDGE,"E5.6.1"),sQuery(id+"F0.wireOp",EDGE,"E5.6.2"),sQuery(id+"F0.wireOp",EDGE,"E5.6.3"),sQuery(id+"F0.wireOp",EDGE,"E5.7.0"),sQuery(id+"F0.wireOp",EDGE,"E5.7.1"),sQuery(id+"F0.wireOp",EDGE,"E5.7.2"),sQuery(id+"F0.wireOp",EDGE,"E5.7.3"),sQuery(id+"F0.wireOp",EDGE,"E5.8.0"),sQuery(id+"F0.wireOp",EDGE,"E5.8.1"),sQuery(id+"F0.wireOp",EDGE,"E5.8.2"),sQuery(id+"F0.wireOp",EDGE,"E5.8.3"),sQuery(id+"F0.wireOp",EDGE,"E5.9.0"),sQuery(id+"F0.wireOp",EDGE,"E5.9.1"),sQuery(id+"F0.wireOp",EDGE,"E5.9.2"),sQuery(id+"F0.wireOp",EDGE,"E5.9.3"),sQuery(id+"F0.wireOp",EDGE,"E5.10.0"),sQuery(id+"F0.wireOp",EDGE,"E5.10.1"),sQuery(id+"F0.wireOp",EDGE,"E5.10.2"),sQuery(id+"F0.wireOp",EDGE,"E5.10.3"),sQuery(id+"F0.wireOp",EDGE,"E5.11.0"),sQuery(id+"F0.wireOp",EDGE,"E5.11.1"),sQuery(id+"F0.wireOp",EDGE,"E5.11.2"),sQuery(id+"F0.wireOp",EDGE,"E5.11.3"),sQuery(id+"F0.wireOp",EDGE,"E5.12.0"),sQuery(id+"F0.wireOp",EDGE,"E5.12.1"),sQuery(id+"F0.wireOp",EDGE,"E5.12.2"),sQuery(id+"F0.wireOp",EDGE,"E5.12.3"),sQuery(id+"F0.wireOp",EDGE,"E5.13.0"),sQuery(id+"F0.wireOp",EDGE,"E5.13.1"),sQuery(id+"F0.wireOp",EDGE,"E5.13.2"),sQuery(id+"F0.wireOp",EDGE,"E5.13.3"),sQuery(id+"F0.wireOp",EDGE,"E5.14.0"),sQuery(id+"F0.wireOp",EDGE,"E5.14.1"),sQuery(id+"F0.wireOp",EDGE,"E5.14.2"),sQuery(id+"F0.wireOp",EDGE,"E5.14.3"),sQuery(id+"F0.wireOp",EDGE,"E5.15.0"),sQuery(id+"F0.wireOp",EDGE,"E5.15.1"),sQuery(id+"F0.wireOp",EDGE,"E5.15.2"),sQuery(id+"F0.wireOp",EDGE,"E5.15.3"),sQuery(id+"F0.wireOp",EDGE,"E5.16.0"),sQuery(id+"F0.wireOp",EDGE,"E5.16.1"),sQuery(id+"F0.wireOp",EDGE,"E5.16.2"),sQuery(id+"F0.wireOp",EDGE,"E5.16.3"),sQuery(id+"F0.wireOp",EDGE,"E5.17.0"),sQuery(id+"F0.wireOp",EDGE,"E5.17.1"),sQuery(id+"F0.wireOp",EDGE,"E5.17.2"),sQuery(id+"F0.wireOp",EDGE,"E5.17.3"),sQuery(id+"F0.wireOp",EDGE,"E5.18.0"),sQuery(id+"F0.wireOp",EDGE,"E5.18.1"),sQuery(id+"F0.wireOp",EDGE,"E5.18.2"),sQuery(id+"F0.wireOp",EDGE,"E5.18.3"),sQuery(id+"F0.wireOp",EDGE,"E5.19.0"),sQuery(id+"F0.wireOp",EDGE,"E5.19.1"),sQuery(id+"F0.wireOp",EDGE,"E5.19.2"),sQuery(id+"F0.wireOp",EDGE,"E5.19.3"),sQuery(id+"F0.wireOp",EDGE,"E5.20.0"),sQuery(id+"F0.wireOp",EDGE,"E5.20.1"),sQuery(id+"F0.wireOp",EDGE,"E5.20.2"),sQuery(id+"F0.wireOp",EDGE,"E5.20.3"),sQuery(id+"F0.wireOp",EDGE,"E5.21.0"),sQuery(id+"F0.wireOp",EDGE,"E5.21.1"),sQuery(id+"F0.wireOp",EDGE,"E5.21.2"),sQuery(id+"F0.wireOp",EDGE,"E5.21.3"),sQuery(id+"F0.wireOp",EDGE,"E5.22.0"),sQuery(id+"F0.wireOp",EDGE,"E5.22.1"),sQuery(id+"F0.wireOp",EDGE,"E5.22.2"),sQuery(id+"F0.wireOp",EDGE,"E5.22.3"),sQuery(id+"F0.wireOp",EDGE,"E5.23.0"),sQuery(id+"F0.wireOp",EDGE,"E5.23.1"),sQuery(id+"F0.wireOp",EDGE,"E5.23.2"),sQuery(id+"F0.wireOp",EDGE,"E5.23.3"),sQuery(id+"F0.wireOp",EDGE,"E5.24.0"),sQuery(id+"F0.wireOp",EDGE,"E5.24.1"),sQuery(id+"F0.wireOp",EDGE,"E5.24.2"),sQuery(id+"F0.wireOp",EDGE,"E5.24.3"),sQuery(id+"F0.wireOp",EDGE,"E5.25.0"),sQuery(id+"F0.wireOp",EDGE,"E5.25.1"),sQuery(id+"F0.wireOp",EDGE,"E5.25.2"),sQuery(id+"F0.wireOp",EDGE,"E5.25.3"),sQuery(id+"F0.wireOp",EDGE,"E5.26.0"),sQuery(id+"F0.wireOp",EDGE,"E5.26.1"),sQuery(id+"F0.wireOp",EDGE,"E5.26.2"),sQuery(id+"F0.wireOp",EDGE,"E5.26.3"),sQuery(id+"F0.wireOp",EDGE,"E5.27.0"),sQuery(id+"F0.wireOp",EDGE,"E5.27.1"),sQuery(id+"F0.wireOp",EDGE,"E5.27.2"),sQuery(id+"F0.wireOp",EDGE,"E5.27.3"),sQuery(id+"F0.wireOp",EDGE,"E5.28.0"),sQuery(id+"F0.wireOp",EDGE,"E5.28.1"),sQuery(id+"F0.wireOp",EDGE,"E5.28.2"),sQuery(id+"F0.wireOp",EDGE,"E5.28.3"),sQuery(id+"F0.wireOp",EDGE,"E5.29.0"),sQuery(id+"F0.wireOp",EDGE,"E5.29.1"),sQuery(id+"F0.wireOp",EDGE,"E5.29.2"),sQuery(id+"F0.wireOp",EDGE,"E5.29.3"),sQuery(id+"F0.wireOp",EDGE,"E5.30.0"),sQuery(id+"F0.wireOp",EDGE,"E5.30.1"),sQuery(id+"F0.wireOp",EDGE,"E5.30.2"),sQuery(id+"F0.wireOp",EDGE,"E5.30.3"),sQuery(id+"F0.wireOp",EDGE,"E5.31.0"),sQuery(id+"F0.wireOp",EDGE,"E5.31.1"),sQuery(id+"F0.wireOp",EDGE,"E5.31.2"),sQuery(id+"F0.wireOp",EDGE,"E5.31.3"),sQuery(id+"F0.wireOp",EDGE,"E5.32.0"),sQuery(id+"F0.wireOp",EDGE,"E5.32.1"),sQuery(id+"F0.wireOp",EDGE,"E5.32.2"),sQuery(id+"F0.wireOp",EDGE,"E5.32.3"),sQuery(id+"F0.wireOp",EDGE,"E5.33.0"),sQuery(id+"F0.wireOp",EDGE,"E5.33.1"),sQuery(id+"F0.wireOp",EDGE,"E5.33.2"),sQuery(id+"F0.wireOp",EDGE,"E5.33.3"),sQuery(id+"F0.wireOp",EDGE,"E5.34.0"),sQuery(id+"F0.wireOp",EDGE,"E5.34.1"),sQuery(id+"F0.wireOp",EDGE,"E5.34.2"),sQuery(id+"F0.wireOp",EDGE,"E5.34.3"),sQuery(id+"F0.wireOp",EDGE,"E5.35.0"),sQuery(id+"F0.wireOp",EDGE,"E5.35.1"),sQuery(id+"F0.wireOp",EDGE,"E5.35.2"),sQuery(id+"F0.wireOp",EDGE,"E5.35.3"),sQuery(id+"F0.wireOp",EDGE,"E6"),sQuery(id+"F0.wireOp",EDGE,"E7.trimOffspring"),sQuery(id+"F0.wireOp",EDGE,"E8.trimOffspring"),sQuery(id+"F0.wireOp",EDGE,"E9.trimOffspring"),sQuery(id+"F0.wireOp",EDGE,"E10.trimOffspring"),sQuery(id+"F0.wireOp",EDGE,"E11.trimOffspring"),sQuery(id+"F0.wireOp",EDGE,"E12.trimOffspring"),sQuery(id+"F0.wireOp",EDGE,"E13.trimOffspring"),sQuery(id+"F0.wireOp",EDGE,"E14.trimOffspring"),sQuery(id+"F0.wireOp",EDGE,"E15.trimOffspring"),sQuery(id+"F0.wireOp",EDGE,"E16.trimOffspring"),sQuery(id+"F0.wireOp",EDGE,"E17.trimOffspring"),sQuery(id+"F0.wireOp",EDGE,"E18.trimOffspring"),sQuery(id+"F0.wireOp",EDGE,"E19.trimOffspring"),sQuery(id+"F0.wireOp",EDGE,"E20.trimOffspring"),sQuery(id+"F0.wireOp",EDGE,"E21.trimOffspring"),sQuery(id+"F0.wireOp",EDGE,"E22.trimOffspring"),sQuery(id+"F0.wireOp",EDGE,"E23.trimOffspring"),sQuery(id+"F0.wireOp",EDGE,"E24.trimOffspring"),sQuery(id+"F0.wireOp",EDGE,"E25.trimOffspring"),sQuery(id+"F0.wireOp",EDGE,"E26.trimOffspring"),sQuery(id+"F0.wireOp",EDGE,"E27.trimOffspring"),sQuery(id+"F0.wireOp",EDGE,"E28.trimOffspring"),sQuery(id+"F0.wireOp",EDGE,"E29.trimOffspring"),sQuery(id+"F0.wireOp",EDGE,"E30.trimOffspring"),sQuery(id+"F0.wireOp",EDGE,"E31.trimOffspring"),sQuery(id+"F0.wireOp",EDGE,"E32.trimOffspring"),sQuery(id+"F0.wireOp",EDGE,"E33.trimOffspring"),sQuery(id+"F0.wireOp",EDGE,"E34.trimOffspring"),sQuery(id+"F0.wireOp",EDGE,"E35.trimOffspring"),sQuery(id+"F0.wireOp",EDGE,"E36.trimOffspring"),sQuery(id+"F0.wireOp",EDGE,"E37.trimOffspring"),sQuery(id+"F0.wireOp",EDGE,"E38.trimOffspring"),sQuery(id+"F0.wireOp",EDGE,"E39.trimOffspring"),sQuery(id+"F0.wireOp",EDGE,"E40.trimOffspring"),sQuery(id+"F0.wireOp",EDGE,"E41.trimOffspring")])],"isStart":false});
            var sketch = newSketch(context, id + "F4", { "sketchPlane" : qUnion([Q0])});
            skCircle(sketch, "E43", {"center": v(0, 12.53) * mm, "radius": 1.76 * mm});
            skSolve(sketch);
        }
        {
            var Q0;
            Q0 = qSketchRegion(id + "F4", true);
            extrude(context, id + "F5", {"entities" : qUnion([Q0]), "operationType" : NewBodyOperationType.REMOVE, "endBound" : BoundingType.THROUGH_ALL, "oppositeDirection" : true, "depth" : 25 * mm, "offsetDistance" : 25 * mm});
        }
    });
